# Revit family: НЕВАТОМ_Щит  тепловых завес с водяным и электрическим калорифером, Версия 1
name_source: partatom
category: Электрооборудование
revit_build: Autodesk Revit 2017 (Build: 20170118_1100(x64)
units: mm (PartAtom-declared; Revit-internal decimal feet)

## family parameters
Всегда вертикально = Да
Конфигурация панели = Два столбца, слева направо
На основе рабочей плоскости = Нет
Общий = Нет
При загрузке вырезать с полостями = Нет
Размер круглого соединителя = Использовать диаметр
Тип детали = Щит
Точка расчета площади = Нет

## types (8) — shared parameters
ADSK_Единица измерения = шт.
ADSK_Завод-изготовитель = НЕВАТОМ
ADSK_Количество = 1
ADSK_Напряжение = 380 В
ADSK_Размер_Высота = 610 мм
ADSK_Размер_Длина = 340 мм
ADSK_Размер_Ширина = 160 мм

## per-type parameters (varying)
| type | НЕВАТОМ_Номинальный ток двигателя | НЕВАТОМ_Ориентировочная мощность двигателя |
| ABU–PVZ–E–1–Z–1,7–15 | 3 А | 2 кВт |
| ABU–PVZ–E–1–Z–2,2–22,5 | 4 А | 2 кВт |
| ABU–PVZ–E–1–Z–3,5–30 | 6 А | 4 кВт |
| ABU–PVZ–W–1–Z–1,7 | 3 А | 2 кВт |
| ABU–PVZ–W–1–Z–2,2 | 4 А | 2 кВт |
| ABU–PVZ–W–1–Z–3,5 | 6 А | 4 кВт |
| ABU–PVZ–W–1–Z–4,8 | 8 А | 5 кВт |
| ABU–PVZ–E–1–Z–4,8–45 | 8 А | 5 кВт |

note: column(s) folded — value = type name in every type: ADSK_Марка, ADSK_Наименование
